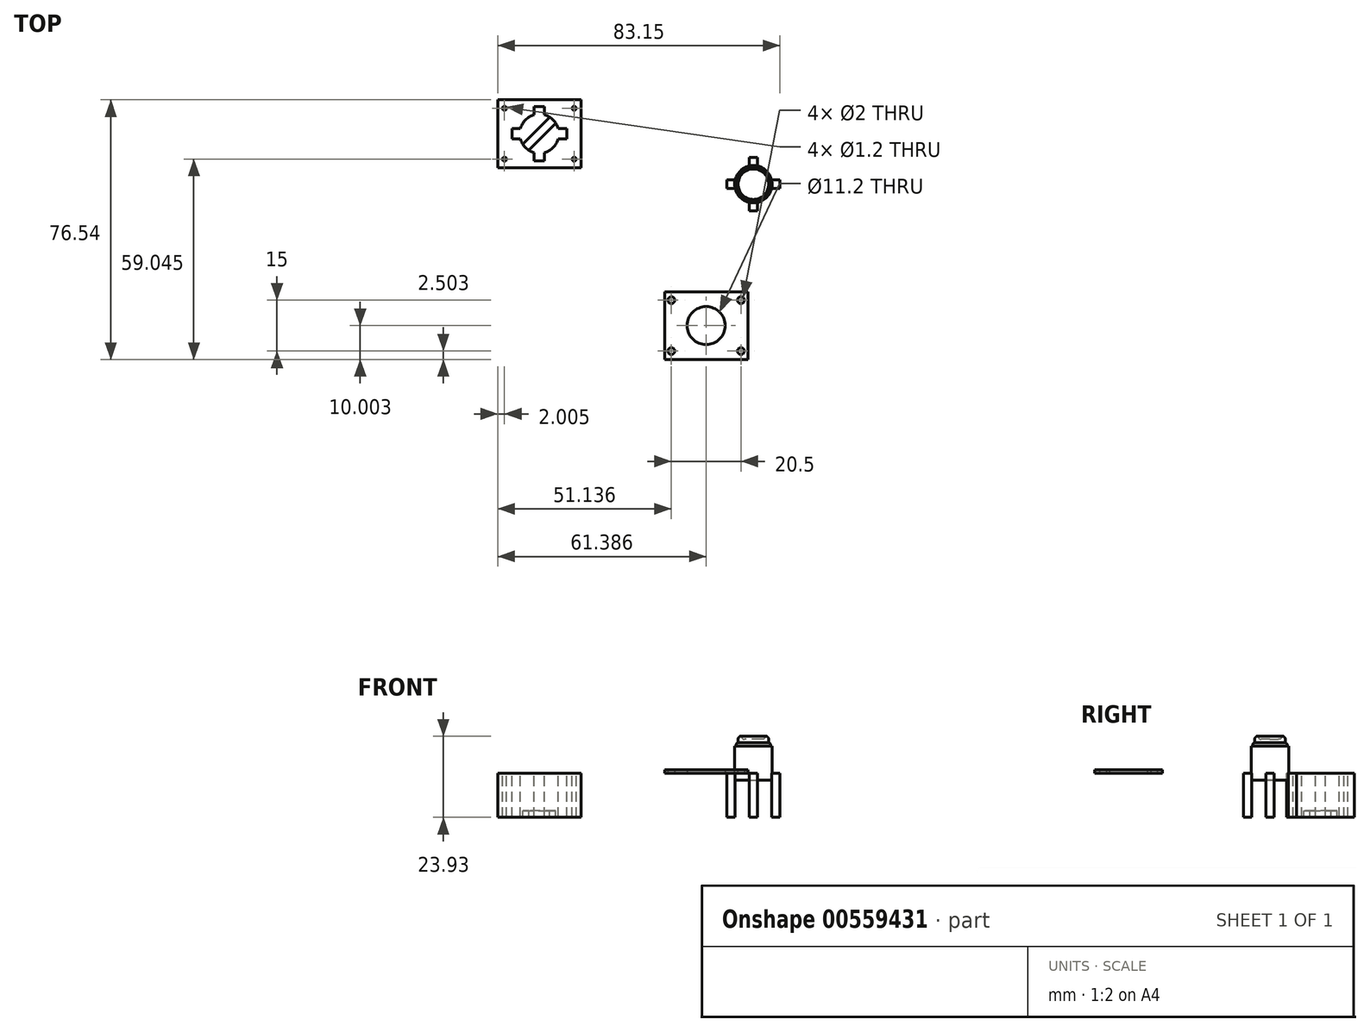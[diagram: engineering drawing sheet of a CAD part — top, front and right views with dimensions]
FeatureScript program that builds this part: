
annotation { "Feature Type Name" : "Feature", "Feature Type Description" : "" }
export const myFeature = defineFeature(function(context is Context, id is Id, definition is map)
    precondition{}
    {
        {
            var Q0;
            Q0=qCreatedBy(makeId("Top.planeOp"),FACE);
            var sketch = newSketch(context, id + "F0", { "sketchPlane" : qUnion([Q0])});
            skCircle(sketch, "E0", {"center": v(-4.33, -178.26) * mm, "radius": 5.75 * mm});
            skCircle(sketch, "E1", {"center": v(-14.58, -170.76) * mm, "radius": 0.6 * mm});
            skCircle(sketch, "E2", {"center": v(5.92, -170.76) * mm, "radius": 0.6 * mm});
            skCircle(sketch, "E3", {"center": v(-14.58, -185.76) * mm, "radius": 0.6 * mm});
            skCircle(sketch, "E4", {"center": v(5.92, -185.76) * mm, "radius": 0.6 * mm});
            skLineSegment(sketch, "E5.bottom", {"start": v(-16.58, -168.26) * mm, "end": v(7.92, -168.26) * mm});
            skLineSegment(sketch, "E5.top", {"start": v(-16.58, -188.26) * mm, "end": v(7.92, -188.26) * mm});
            skLineSegment(sketch, "E5.left", {"start": v(-16.58, -168.26) * mm, "end": v(-16.58, -188.26) * mm});
            skLineSegment(sketch, "E5.right", {"start": v(7.92, -168.26) * mm, "end": v(7.92, -188.26) * mm});
            skLineSegment(sketch, "E6.bottom", {"start": v(-12.38, -176.76) * mm, "end": v(-9.88, -176.76) * mm});
            skLineSegment(sketch, "E6.top", {"start": v(-12.38, -179.76) * mm, "end": v(-9.88, -179.76) * mm});
            skLineSegment(sketch, "E6.left", {"start": v(-12.38, -176.76) * mm, "end": v(-12.38, -179.76) * mm});
            skLineSegment(sketch, "E6.right", {"start": v(-9.88, -176.76) * mm, "end": v(-9.88, -179.76) * mm});
            skLineSegment(sketch, "E7.bottom", {"start": v(1.23, -176.76) * mm, "end": v(3.73, -176.76) * mm});
            skLineSegment(sketch, "E7.top", {"start": v(1.23, -179.76) * mm, "end": v(3.73, -179.76) * mm});
            skLineSegment(sketch, "E7.left", {"start": v(1.23, -176.76) * mm, "end": v(1.23, -179.76) * mm});
            skLineSegment(sketch, "E7.right", {"start": v(3.73, -176.76) * mm, "end": v(3.73, -179.76) * mm});
            skLineSegment(sketch, "E8.bottom", {"start": v(-5.83, -170.2) * mm, "end": v(-2.83, -170.2) * mm});
            skLineSegment(sketch, "E8.top", {"start": v(-5.83, -172.7) * mm, "end": v(-2.83, -172.7) * mm});
            skLineSegment(sketch, "E8.left", {"start": v(-5.83, -170.2) * mm, "end": v(-5.83, -172.7) * mm});
            skLineSegment(sketch, "E8.right", {"start": v(-2.83, -170.2) * mm, "end": v(-2.83, -172.7) * mm});
            skLineSegment(sketch, "E9.bottom", {"start": v(-5.83, -183.8) * mm, "end": v(-2.83, -183.8) * mm});
            skLineSegment(sketch, "E9.top", {"start": v(-5.83, -186.3) * mm, "end": v(-2.83, -186.3) * mm});
            skLineSegment(sketch, "E9.left", {"start": v(-5.83, -183.8) * mm, "end": v(-5.83, -186.3) * mm});
            skLineSegment(sketch, "E9.right", {"start": v(-2.83, -183.8) * mm, "end": v(-2.83, -186.3) * mm});
            skSolve(sketch);
        }
        {
            var Q0;
            Q0=makeQuery(id+"F0.imprint","IMPRINT",FACE,{"disambiguationData":[TD([[makeQuery(id+"F0.imprint","IMPRINT",EDGE,{"derivedFrom":sQuery(id+"F0.wireOp",EDGE,"E1")}),-1.0]])]});
            extrude(context, id + "F1", {"entities" : qUnion([Q0]), "oppositeDirection" : true, "depth" : 13 * mm});
        }
        {
            var Q0;
            Q0=makeQuery(id+"F1.opExtrude","CAP_FACE",FACE,{"disambiguationData":[OSD([sQuery(id+"F0.wireOp",EDGE,"E0"),sQuery(id+"F0.wireOp",EDGE,"E1"),sQuery(id+"F0.wireOp",EDGE,"E2"),sQuery(id+"F0.wireOp",EDGE,"E3"),sQuery(id+"F0.wireOp",EDGE,"E4"),sQuery(id+"F0.wireOp",EDGE,"E5.bottom"),sQuery(id+"F0.wireOp",EDGE,"E5.top"),sQuery(id+"F0.wireOp",EDGE,"E5.left"),sQuery(id+"F0.wireOp",EDGE,"E5.right"),sQuery(id+"F0.wireOp",EDGE,"E6.bottom"),sQuery(id+"F0.wireOp",EDGE,"E6.top"),sQuery(id+"F0.wireOp",EDGE,"E6.left"),sQuery(id+"F0.wireOp",EDGE,"E7.bottom"),sQuery(id+"F0.wireOp",EDGE,"E7.top"),sQuery(id+"F0.wireOp",EDGE,"E7.right"),sQuery(id+"F0.wireOp",EDGE,"E8.bottom"),sQuery(id+"F0.wireOp",EDGE,"E8.left"),sQuery(id+"F0.wireOp",EDGE,"E8.right"),sQuery(id+"F0.wireOp",EDGE,"E9.top"),sQuery(id+"F0.wireOp",EDGE,"E9.left"),sQuery(id+"F0.wireOp",EDGE,"E9.right")])],"isStart":false});
            var sketch = newSketch(context, id + "F2", { "sketchPlane" : qUnion([Q0])});
            skLineSegment(sketch, "E10", {"start": v(-9.45, 181.61) * mm, "end": v(-0.97, 173.13) * mm});
            skLineSegment(sketch, "E11", {"start": v(-0.97, 173.13) * mm, "end": v(0.8, 174.9) * mm});
            skLineSegment(sketch, "E12", {"start": v(0.8, 174.9) * mm, "end": v(-7.68, 183.38) * mm});
            skLineSegment(sketch, "E13", {"start": v(-7.68, 183.38) * mm, "end": v(-9.45, 181.61) * mm});
            skSolve(sketch);
        }
        {
            var Q0;
            Q0=qSketchRegion(id+"F2",true);
            extrude(context, id + "F3", {"entities" : qUnion([Q0]), "operationType" : NewBodyOperationType.ADD, "oppositeDirection" : true, "depth" : 2 * mm});
        }
        {
            var Q0;
            Q0=qCreatedBy(makeId("Top.planeOp"),FACE);
            var sketch = newSketch(context, id + "F4", { "sketchPlane" : qUnion([Q0])});
            skCircle(sketch, "E14", {"center": v(34.4, -175.93) * mm, "radius": 5.5 * mm});
            skLineSegment(sketch, "E15.bottom", {"start": v(29.04, -177.18) * mm, "end": v(26.54, -177.18) * mm});
            skLineSegment(sketch, "E15.top", {"start": v(29.04, -174.68) * mm, "end": v(26.54, -174.68) * mm});
            skLineSegment(sketch, "E15.left", {"start": v(29.04, -177.18) * mm, "end": v(29.04, -174.68) * mm});
            skLineSegment(sketch, "E15.right", {"start": v(26.54, -177.18) * mm, "end": v(26.54, -174.68) * mm});
            skPoint(sketch, "E15.middle", {"position": v(27.8, -175.93) * mm});
            skLineSegment(sketch, "E16", {"start": v(34.4, -170.43) * mm, "end": v(23.26, -170.43) * mm, "construction": true});
            skLineSegment(sketch, "E17", {"start": v(34.4, -181.43) * mm, "end": v(44.12, -181.43) * mm, "construction": true});
            skLineSegment(sketch, "E18.bottom", {"start": v(39.75, -174.68) * mm, "end": v(42.25, -174.68) * mm});
            skLineSegment(sketch, "E18.top", {"start": v(39.75, -177.18) * mm, "end": v(42.25, -177.18) * mm});
            skLineSegment(sketch, "E18.left", {"start": v(39.75, -174.68) * mm, "end": v(39.75, -177.18) * mm});
            skLineSegment(sketch, "E18.right", {"start": v(42.25, -174.68) * mm, "end": v(42.25, -177.18) * mm});
            skLineSegment(sketch, "E19.bottom", {"start": v(33.15, -168.08) * mm, "end": v(35.65, -168.08) * mm});
            skLineSegment(sketch, "E19.top", {"start": v(33.15, -170.58) * mm, "end": v(35.65, -170.58) * mm});
            skLineSegment(sketch, "E19.left", {"start": v(33.15, -168.08) * mm, "end": v(33.15, -170.58) * mm});
            skLineSegment(sketch, "E19.right", {"start": v(35.65, -168.08) * mm, "end": v(35.65, -170.58) * mm});
            skLineSegment(sketch, "E20.bottom", {"start": v(33.15, -181.3) * mm, "end": v(35.65, -181.3) * mm});
            skLineSegment(sketch, "E20.top", {"start": v(33.15, -183.8) * mm, "end": v(35.65, -183.8) * mm});
            skLineSegment(sketch, "E20.left", {"start": v(33.15, -181.3) * mm, "end": v(33.15, -183.8) * mm});
            skLineSegment(sketch, "E20.right", {"start": v(35.65, -181.3) * mm, "end": v(35.65, -183.8) * mm});
            skLineSegment(sketch, "E21.bottom", {"start": v(53.35, -194.38) * mm, "end": v(50.85, -194.38) * mm});
            skLineSegment(sketch, "E21.top", {"start": v(53.35, -191.88) * mm, "end": v(50.85, -191.88) * mm});
            skLineSegment(sketch, "E21.left", {"start": v(53.35, -194.38) * mm, "end": v(53.35, -191.88) * mm});
            skLineSegment(sketch, "E21.right", {"start": v(50.85, -194.38) * mm, "end": v(50.85, -191.88) * mm});
            skLineSegment(sketch, "E22", {"start": v(58.7, -187.63) * mm, "end": v(47.57, -187.63) * mm, "construction": true});
            skLineSegment(sketch, "E23", {"start": v(58.7, -198.63) * mm, "end": v(68.43, -198.63) * mm, "construction": true});
            skLineSegment(sketch, "E24.bottom", {"start": v(64.07, -191.88) * mm, "end": v(66.57, -191.88) * mm});
            skLineSegment(sketch, "E24.top", {"start": v(64.07, -194.38) * mm, "end": v(66.57, -194.38) * mm});
            skLineSegment(sketch, "E24.left", {"start": v(64.07, -191.88) * mm, "end": v(64.07, -194.38) * mm});
            skLineSegment(sketch, "E24.right", {"start": v(66.57, -191.88) * mm, "end": v(66.57, -194.38) * mm});
            skLineSegment(sketch, "E25.bottom", {"start": v(57.46, -185.28) * mm, "end": v(59.96, -185.28) * mm});
            skLineSegment(sketch, "E25.top", {"start": v(57.46, -187.78) * mm, "end": v(59.96, -187.78) * mm});
            skLineSegment(sketch, "E25.left", {"start": v(57.46, -185.28) * mm, "end": v(57.46, -187.78) * mm});
            skLineSegment(sketch, "E25.right", {"start": v(59.96, -185.28) * mm, "end": v(59.96, -187.78) * mm});
            skLineSegment(sketch, "E26.bottom", {"start": v(57.46, -198.49) * mm, "end": v(59.96, -198.49) * mm});
            skLineSegment(sketch, "E26.top", {"start": v(57.46, -200.99) * mm, "end": v(59.96, -200.99) * mm});
            skLineSegment(sketch, "E26.left", {"start": v(57.46, -198.49) * mm, "end": v(57.46, -200.99) * mm});
            skLineSegment(sketch, "E26.right", {"start": v(59.96, -198.49) * mm, "end": v(59.96, -200.99) * mm});
            skLineSegment(sketch, "E27", {"start": v(69.57, -185.18) * mm, "end": v(69.57, -200) * mm, "construction": true});
            skLineSegment(sketch, "E28", {"start": v(48.35, -186.36) * mm, "end": v(48.35, -199.94) * mm, "construction": true});
            skSolve(sketch);
        }
        {
            var Q0;
            Q0=makeQuery(id+"F4.imprint","IMPRINT",FACE,{"disambiguationData":[TD([[makeQuery(id+"F4.imprint","IMPRINT",EDGE,{"derivedFrom":sQuery(id+"F4.wireOp",EDGE,"E25.bottom")}),-1.0]])]});
            var sketch = newSketch(context, id + "F5", { "sketchPlane" : qUnion([Q0])});
            skCircle(sketch, "E29", {"center": v(58.7, -193.13) * mm, "radius": 5.5 * mm});
            skSolve(sketch);
        }
        {
            var Q0;
            {var subQ0=sQuery(id+"F5.wireOp",EDGE,"E29");var subQ1=makeQuery(id+"F4.imprint","IMPRINT",EDGE,{"derivedFrom":sQuery(id+"F4.wireOp",EDGE,"E25.top")});var subQ3=makeQuery(id+"F5.imprint","INTERSECT",VERTEX,{"derivedFrom":[subQ1,subQ0]});Q0=makeQuery(id+"F5.imprint","IMPRINT",FACE,{"disambiguationData":[TD([[makeQuery(id+"F5.imprint","IMPRINT",EDGE,{"disambiguationData":[TD([[subQ3,-1.0]])],"derivedFrom":subQ0}),1.0]])]});}
            extrude(context, id + "F6", {"entities" : qUnion([Q0]), "oppositeDirection" : true, "depth" : 2 * mm});
        }
        {
            var Q0;
            Q0=makeQuery(id+"F4.imprint","IMPRINT",FACE,{"disambiguationData":[TD([[makeQuery(id+"F4.imprint","IMPRINT",EDGE,{"derivedFrom":sQuery(id+"F4.wireOp",EDGE,"E21.bottom")}),-1.0]])]});
            var Q1;
            Q1=makeQuery(id+"F4.imprint","IMPRINT",FACE,{"disambiguationData":[TD([[makeQuery(id+"F4.imprint","IMPRINT",EDGE,{"derivedFrom":sQuery(id+"F4.wireOp",EDGE,"E25.bottom")}),-1.0]])]});
            var Q2;
            Q2=makeQuery(id+"F4.imprint","IMPRINT",FACE,{"disambiguationData":[TD([[makeQuery(id+"F4.imprint","IMPRINT",EDGE,{"derivedFrom":sQuery(id+"F4.wireOp",EDGE,"E24.bottom")}),-1.0]])]});
            var Q3;
            Q3=makeQuery(id+"F4.imprint","IMPRINT",FACE,{"disambiguationData":[TD([[makeQuery(id+"F4.imprint","IMPRINT",EDGE,{"derivedFrom":sQuery(id+"F4.wireOp",EDGE,"E26.bottom")}),-1.0]])]});
            extrude(context, id + "F7", {"entities" : qUnion([Q0, Q1, Q2, Q3]), "operationType" : NewBodyOperationType.ADD, "oppositeDirection" : true, "depth" : 13 * mm});
        }
        {
            var Q0;
            {var subQ0=sQuery(id+"F5.wireOp",EDGE,"E29");var subQ1=makeQuery(id+"F4.imprint","IMPRINT",EDGE,{"derivedFrom":sQuery(id+"F4.wireOp",EDGE,"E25.top")});var subQ3=makeQuery(id+"F5.imprint","INTERSECT",VERTEX,{"derivedFrom":[subQ1,subQ0]});Q0=makeQuery(id+"F5.imprint","IMPRINT",FACE,{"disambiguationData":[TD([[makeQuery(id+"F5.imprint","IMPRINT",EDGE,{"disambiguationData":[TD([[subQ3,-1.0]])],"derivedFrom":subQ0}),1.0]])]});}
            var Q1;
            {var subQ0=sQuery(id+"F5.wireOp",EDGE,"E29");var subQ1=makeQuery(id+"F4.imprint","IMPRINT",EDGE,{"derivedFrom":sQuery(id+"F4.wireOp",EDGE,"E25.top")});var subQ3=makeQuery(id+"F5.imprint","INTERSECT",VERTEX,{"derivedFrom":[subQ1,subQ0]});Q1=makeQuery(id+"F5.imprint","IMPRINT",FACE,{"disambiguationData":[TD([[makeQuery(id+"F5.imprint","IMPRINT",EDGE,{"disambiguationData":[TD([[subQ3,1.0]])],"derivedFrom":subQ0}),1.0]])]});}
            extrude(context, id + "F8", {"entities" : qUnion([Q0, Q1]), "operationType" : NewBodyOperationType.ADD, "depth" : 8 * mm});
        }
        {
            var Q0;
            Q0=makeQuery(id+"F8.opExtrude","CAP_FACE",FACE,{"disambiguationData":[OSD([sQuery(id+"F5.wireOp",EDGE,"E29")])],"isStart":false});
            var sketch = newSketch(context, id + "F9", { "sketchPlane" : qUnion([Q0])});
            skCircle(sketch, "E30", {"center": v(58.7, -193.13) * mm, "radius": 5 * mm});
            skSolve(sketch);
        }
        {
            var Q0;
            Q0=qSketchRegion(id+"F9",true);
            extrude(context, id + "F10", {"entities" : qUnion([Q0]), "operationType" : NewBodyOperationType.ADD, "depth" : 1 * mm});
        }
        {
            var Q0;
            Q0=makeQuery(id+"F10.opExtrude","CAP_FACE",FACE,{"disambiguationData":[OSD([sQuery(id+"F9.wireOp",EDGE,"E30")])],"isStart":false});
            var sketch = newSketch(context, id + "F11", { "sketchPlane" : qUnion([Q0])});
            skCircle(sketch, "E31", {"center": v(58.7, -193.13) * mm, "radius": 4.5 * mm});
            skSolve(sketch);
        }
        {
            var Q0;
            Q0=makeQuery(id+"F11.imprint","IMPRINT",FACE,{"disambiguationData":[TD([[makeQuery(id+"F11.imprint","IMPRINT",EDGE,{"derivedFrom":sQuery(id+"F11.wireOp",EDGE,"E31")}),1.0]])]});
            extrude(context, id + "F12", {"entities" : qUnion([Q0]), "operationType" : NewBodyOperationType.ADD, "depth" : 2 * mm});
        }
        {
            var Q0;
            Q0=makeQuery(id+"F10.opExtrude","CAP_EDGE",EDGE,{"disambiguationData":[OSD([sQuery(id+"F9.wireOp",EDGE,"E30")])],"isStart":false});
            fillet(context, id + "F13", {"entities" : qUnion([Q0]), "radius" : 0.5 * mm, "tangentPropagation" : true, "allowEdgeOverflow" : false});
        }
        {
            var Q0;
            Q0=makeQuery(id+"F12.opExtrude","CAP_EDGE",EDGE,{"disambiguationData":[OSD([sQuery(id+"F11.wireOp",EDGE,"E31")])],"isStart":false});
            fillet(context, id + "F14", {"entities" : qUnion([Q0]), "radius" : 1 * mm, "tangentPropagation" : true, "allowEdgeOverflow" : false});
        }
        {
            var Q0;
            Q0=makeQuery(id+"F12.opExtrude","CAP_FACE",FACE,{"disambiguationData":[OSD([sQuery(id+"F11.wireOp",EDGE,"E31")])],"isStart":false});
            extrude(context, id + "F15", {"entities" : qUnion([Q0]), "operationType" : NewBodyOperationType.REMOVE, "oppositeDirection" : true, "depth" : 1 * mm});
        }
        {
            var Q0;
            {var subQ0=sQuery(id+"F11.wireOp",EDGE,"E31");Q0=makeQuery(id+"F15.boolean.opBoolean","MERGE",EDGE,{"derivedFrom":[makeQuery(id+"F14.opFillet","BLEND_EDGE",EDGE,{"blendedFrom":[makeQuery(id+"F12.opExtrude","CAP_EDGE",EDGE,{"disambiguationData":[OSD([subQ0])],"isStart":false}),makeQuery(id+"F12.opExtrude","CAP_FACE",FACE,{"disambiguationData":[OSD([subQ0])],"isStart":false})],"blendedInto":[makeQuery(id+"F12.opExtrude","CAP_FACE",FACE,{"disambiguationData":[OSD([subQ0])],"isStart":false})]}),makeQuery(id+"F15.opExtrude","CAP_EDGE",EDGE,{"disambiguationData":[OSD([subQ0])],"isStart":true})]});}
            fillet(context, id + "F16", {"entities" : qUnion([Q0]), "radius" : 0.3 * mm, "tangentPropagation" : true, "allowEdgeOverflow" : false});
        }
        {
            var Q0;
            Q0=makeQuery(id+"F15.boolean.opBoolean","COPY",EDGE,{"derivedFrom":makeQuery(id+"F15.opExtrude","CAP_EDGE",EDGE,{"disambiguationData":[OSD([sQuery(id+"F11.wireOp",EDGE,"E31")])],"isStart":false})});
            fillet(context, id + "F17", {"entities" : qUnion([Q0]), "radius" : 1 * mm, "tangentPropagation" : true, "allowEdgeOverflow" : false});
        }
        {
            var Q0;
            Q0=qCreatedBy(makeId("Top.planeOp"),FACE);
            var sketch = newSketch(context, id + "F18", { "sketchPlane" : qUnion([Q0])});
            skCircle(sketch, "E32", {"center": v(34.56, -227.3) * mm, "radius": 1 * mm});
            skCircle(sketch, "E33", {"center": v(55.06, -227.3) * mm, "radius": 1 * mm});
            skCircle(sketch, "E34", {"center": v(34.56, -242.3) * mm, "radius": 1 * mm});
            skCircle(sketch, "E35", {"center": v(55.06, -242.3) * mm, "radius": 1 * mm});
            skLineSegment(sketch, "E36.bottom", {"start": v(32.56, -224.8) * mm, "end": v(57.06, -224.8) * mm});
            skLineSegment(sketch, "E36.top", {"start": v(32.56, -244.8) * mm, "end": v(57.06, -244.8) * mm});
            skLineSegment(sketch, "E36.left", {"start": v(32.56, -224.8) * mm, "end": v(32.56, -244.8) * mm});
            skLineSegment(sketch, "E36.right", {"start": v(57.06, -224.8) * mm, "end": v(57.06, -244.8) * mm});
            skCircle(sketch, "E37", {"center": v(44.8, -234.8) * mm, "radius": 5.6 * mm});
            skSolve(sketch);
        }
        {
            var Q0;
            Q0=makeQuery(id+"F18.imprint","IMPRINT",FACE,{"disambiguationData":[TD([[makeQuery(id+"F18.imprint","IMPRINT",EDGE,{"derivedFrom":sQuery(id+"F18.wireOp",EDGE,"E32")}),-1.0]])]});
            extrude(context, id + "F19", {"entities" : qUnion([Q0]), "depth" : 1 * mm});
        }
    });
